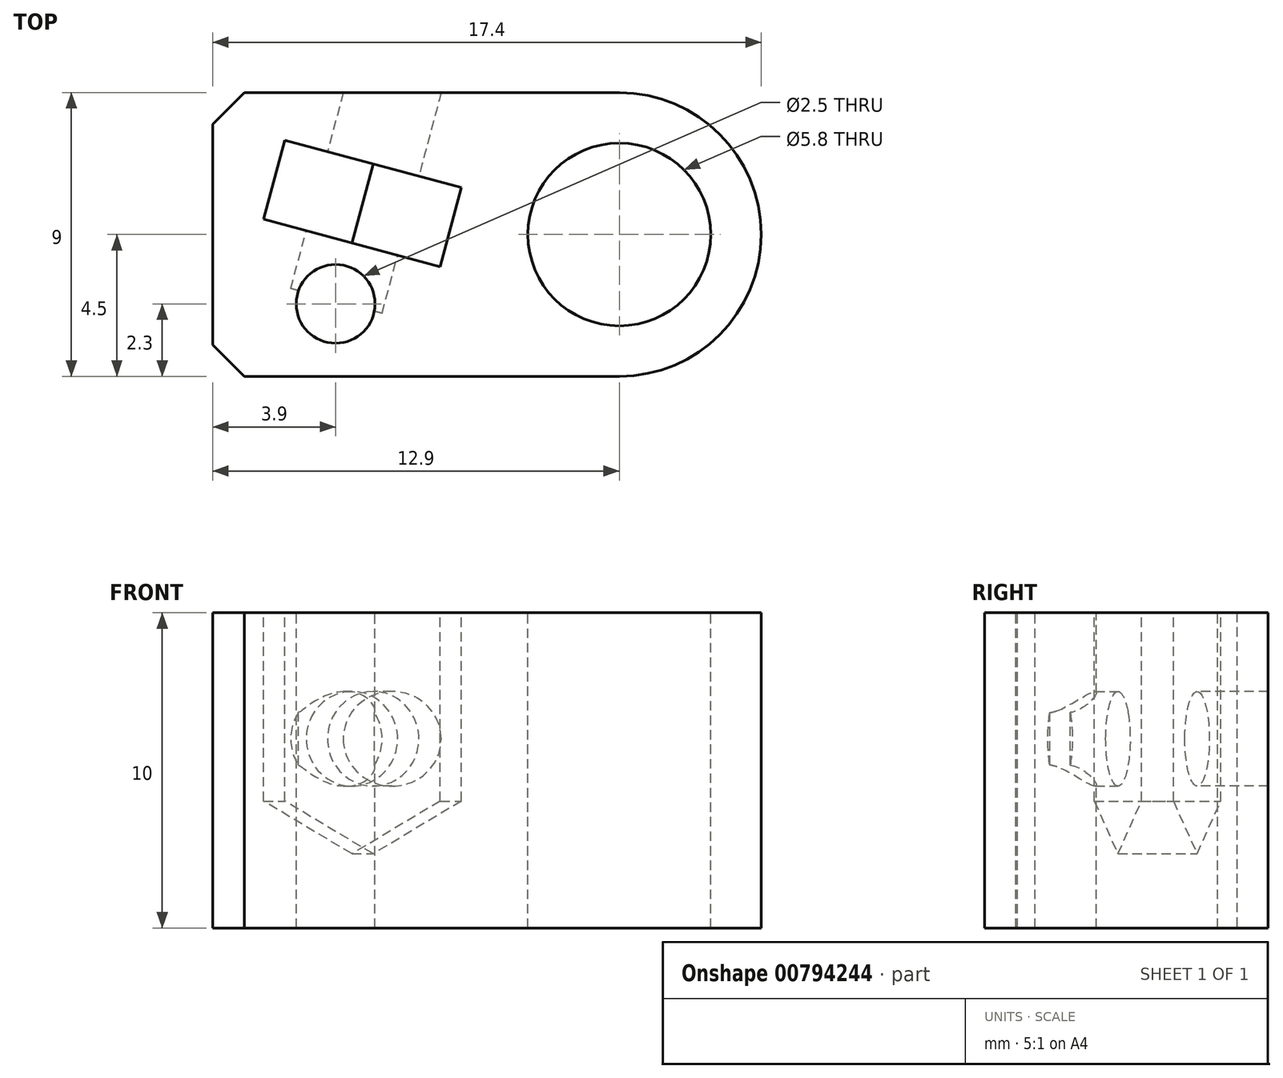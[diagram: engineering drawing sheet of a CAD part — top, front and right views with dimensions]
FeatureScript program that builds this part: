
annotation { "Feature Type Name" : "Feature", "Feature Type Description" : "" }
export const myFeature = defineFeature(function(context is Context, id is Id, definition is map)
    precondition{}
    {
        {
            var Q0;
            Q0=qCreatedBy(makeId("Top.planeOp"),FACE);
            var sketch = newSketch(context, id + "F0", { "sketchPlane" : qUnion([Q0])});
            skLineSegment(sketch, "E0.bottom", {"start": v(0, 0) * mm, "end": v(12.9, 0) * mm});
            skLineSegment(sketch, "E0.top", {"start": v(0, 9) * mm, "end": v(12.9, 9) * mm});
            skLineSegment(sketch, "E0.left", {"start": v(0, 0) * mm, "end": v(0, 9) * mm});
            skLineSegment(sketch, "E0.right", {"start": v(12.9, 0) * mm, "end": v(12.9, 9) * mm});
            skCircle(sketch, "E1", {"center": v(12.9, 4.5) * mm, "radius": 4.5 * mm});
            skCircle(sketch, "E2", {"center": v(12.9, 4.5) * mm, "radius": 2.9 * mm});
            skCircle(sketch, "E3", {"center": v(3.9, 2.3) * mm, "radius": 1.25 * mm});
            skSolve(sketch);
        }
        {
            var Q0;
            Q0 = qSketchRegion(id + "F0", true);
            extrude(context, id + "F1", {"entities" : qUnion([Q0]), "oppositeDirection" : true, "depth" : 10 * mm, "offsetDistance" : 25 * mm});
        }
        {
            var Q0;
            Q0=makeQuery(id+"F1.opExtrude","CAP_FACE",FACE,{"disambiguationData":[OSD([sQuery(id+"F0.wireOp",EDGE,"E0.bottom"),sQuery(id+"F0.wireOp",EDGE,"E0.top"),sQuery(id+"F0.wireOp",EDGE,"E0.left"),sQuery(id+"F0.wireOp",EDGE,"E1"),sQuery(id+"F0.wireOp",EDGE,"E2"),sQuery(id+"F0.wireOp",EDGE,"E3")])],"isStart":true});
            var sketch = newSketch(context, id + "F2", { "sketchPlane" : qUnion([Q0])});
            skLineSegment(sketch, "E4.bottom", {"start": v(2.29, 7.5) * mm, "end": v(7.9, 6) * mm});
            skLineSegment(sketch, "E4.top", {"start": v(1.62, 4.98) * mm, "end": v(7.22, 3.48) * mm});
            skLineSegment(sketch, "E4.left", {"start": v(2.29, 7.5) * mm, "end": v(1.62, 4.98) * mm});
            skLineSegment(sketch, "E4.right", {"start": v(7.9, 6) * mm, "end": v(7.22, 3.48) * mm});
            skPoint(sketch, "E5", {"position": v(3.9, 2.3) * mm});
            skLineSegment(sketch, "E6", {"start": v(1.18, 2.3) * mm, "end": v(6.9, 2.3) * mm, "construction": true});
            skLineSegment(sketch, "E7", {"start": v(3.9, 2.3) * mm, "end": v(4.42, 4.23) * mm, "construction": true});
            skSolve(sketch);
        }
        {
            var Q0;
            Q0=makeQuery(id+"F2.imprint","IMPRINT",FACE,{"disambiguationData":[TD([[makeQuery(id+"F2.imprint","IMPRINT",EDGE,{"derivedFrom":sQuery(id+"F2.wireOp",EDGE,"E4.bottom")}),-1.0]])]});
            extrude(context, id + "F3", {"entities" : qUnion([Q0]), "operationType" : NewBodyOperationType.REMOVE, "oppositeDirection" : true, "depth" : 5 * mm, "offsetDistance" : 25 * mm});
        }
        {
            var Q0;
            Q0=makeQuery(id+"F3.boolean.opBoolean","COPY",FACE,{"derivedFrom":makeQuery(id+"F3.opExtrude","SWEPT_FACE",FACE,{"disambiguationData":[OSD([sQuery(id+"F2.wireOp",EDGE,"E4.bottom")])]})});
            var sketch = newSketch(context, id + "F4", { "sketchPlane" : qUnion([Q0])});
            skLineSegment(sketch, "E8.bottom", {"start": v(0.27, 0) * mm, "end": v(6.07, 0) * mm, "construction": true});
            skLineSegment(sketch, "E8.left", {"start": v(0.27, 0) * mm, "end": v(0.27, -5) * mm, "construction": true});
            skLineSegment(sketch, "E8.right", {"start": v(6.07, 0) * mm, "end": v(6.07, -5) * mm, "construction": true});
            skCircle(sketch, "E9.cCircle", {"center": v(3.17, -4.3) * mm, "radius": 2.9 * mm, "construction": true});
            skPoint(sketch, "E9.cCircle.centerSnap0", {"position": v(3.17, -5) * mm});
            skLineSegment(sketch, "E9.0", {"start": v(6.07, -2.63) * mm, "end": v(6.07, -5.97) * mm});
            skLineSegment(sketch, "E9.1", {"start": v(6.07, -5.97) * mm, "end": v(3.17, -7.65) * mm});
            skLineSegment(sketch, "E9.2", {"start": v(3.17, -7.65) * mm, "end": v(0.27, -5.97) * mm});
            skLineSegment(sketch, "E9.3", {"start": v(0.27, -5.97) * mm, "end": v(0.27, -2.63) * mm});
            skLineSegment(sketch, "E9.4", {"start": v(0.27, -2.63) * mm, "end": v(3.17, -0.95) * mm});
            skLineSegment(sketch, "E9.5", {"start": v(3.17, -0.95) * mm, "end": v(6.07, -2.63) * mm});
            skPoint(sketch, "E9.0.midPoint", {"position": v(6.07, -4.3) * mm});
            skSolve(sketch);
        }
        {
            var Q0;
            Q0 = qSketchRegion(id + "F4", true);
            var Q1;
            Q1=makeQuery(id+"F3.boolean.opBoolean","COPY",VERTEX,{"derivedFrom":makeQuery(id+"F3.opExtrude","CAP_VERTEX",VERTEX,{"disambiguationData":[OSD([sQuery(id+"F2.wireOp",EDGE,"E4.top"),sQuery(id+"F2.wireOp",EDGE,"E4.right")])],"isStart":false})});
            extrude(context, id + "F5", {"entities" : qUnion([Q0]), "operationType" : NewBodyOperationType.REMOVE, "endBound" : BoundingType.UP_TO_VERTEX, "depth" : 25 * mm, "endBoundEntityVertex" : qUnion([Q1]), "offsetDistance" : 25 * mm});
        }
        {
            var Q0;
            Q0=makeQuery(id+"F5.boolean.opBoolean","MERGE",FACE,{"derivedFrom":[makeQuery(id+"F3.boolean.opBoolean","COPY",FACE,{"derivedFrom":makeQuery(id+"F3.opExtrude","SWEPT_FACE",FACE,{"disambiguationData":[OSD([sQuery(id+"F2.wireOp",EDGE,"E4.bottom")])]})}),makeQuery(id+"F5.opExtrude","CAP_FACE",FACE,{"disambiguationData":[OSD([sQuery(id+"F4.wireOp",EDGE,"E9.0"),sQuery(id+"F4.wireOp",EDGE,"E9.1"),sQuery(id+"F4.wireOp",EDGE,"E9.2"),sQuery(id+"F4.wireOp",EDGE,"E9.3"),sQuery(id+"F4.wireOp",EDGE,"E9.4"),sQuery(id+"F4.wireOp",EDGE,"E9.5")])],"isStart":true})]});
            var sketch = newSketch(context, id + "F6", { "sketchPlane" : qUnion([Q0])});
            skLineSegment(sketch, "E10.bottom", {"start": v(0.27, 0) * mm, "end": v(6.07, 0) * mm, "construction": true});
            skLineSegment(sketch, "E10.top", {"start": v(0.27, -5.97) * mm, "end": v(6.07, -5.97) * mm, "construction": true});
            skLineSegment(sketch, "E10.left", {"start": v(0.27, 0) * mm, "end": v(0.27, -5.97) * mm, "construction": true});
            skLineSegment(sketch, "E10.right", {"start": v(6.07, 0) * mm, "end": v(6.07, -5.97) * mm, "construction": true});
            skLineSegment(sketch, "E11", {"start": v(3.17, 0) * mm, "end": v(3.17, -5.97) * mm, "construction": true});
            skCircle(sketch, "E12", {"center": v(3.17, -4) * mm, "radius": 1.5 * mm});
            skSolve(sketch);
        }
        {
            var Q0;
            Q0 = qSketchRegion(id + "F6", true);
            extrude(context, id + "F7", {"entities" : qUnion([Q0]), "operationType" : NewBodyOperationType.REMOVE, "oppositeDirection" : true, "depth" : 3 * mm, "offsetDistance" : 25 * mm});
        }
        {
            var Q0;
            Q0 = qSketchRegion(id + "F6", true);
            extrude(context, id + "F8", {"entities" : qUnion([Q0]), "operationType" : NewBodyOperationType.REMOVE, "depth" : 4.5 * mm, "offsetDistance" : 25 * mm});
        }
        {
            var Q0;
            Q0=makeQuery(id+"F1.opExtrude","SWEPT_EDGE",EDGE,{"disambiguationData":[OSD([sQuery(id+"F0.wireOp",EDGE,"E0.bottom"),sQuery(id+"F0.wireOp",EDGE,"E0.left")])]});
            chamfer(context, id + "F9", {"entities" : qUnion([Q0]), "width" : 1 * mm, "tangentPropagation" : true});
        }
        {
            var Q0;
            Q0=makeQuery(id+"F1.opExtrude","SWEPT_EDGE",EDGE,{"disambiguationData":[OSD([sQuery(id+"F0.wireOp",EDGE,"E0.top"),sQuery(id+"F0.wireOp",EDGE,"E0.left")])]});
            chamfer(context, id + "F10", {"entities" : qUnion([Q0]), "width" : 1 * mm, "tangentPropagation" : true});
        }
    });
